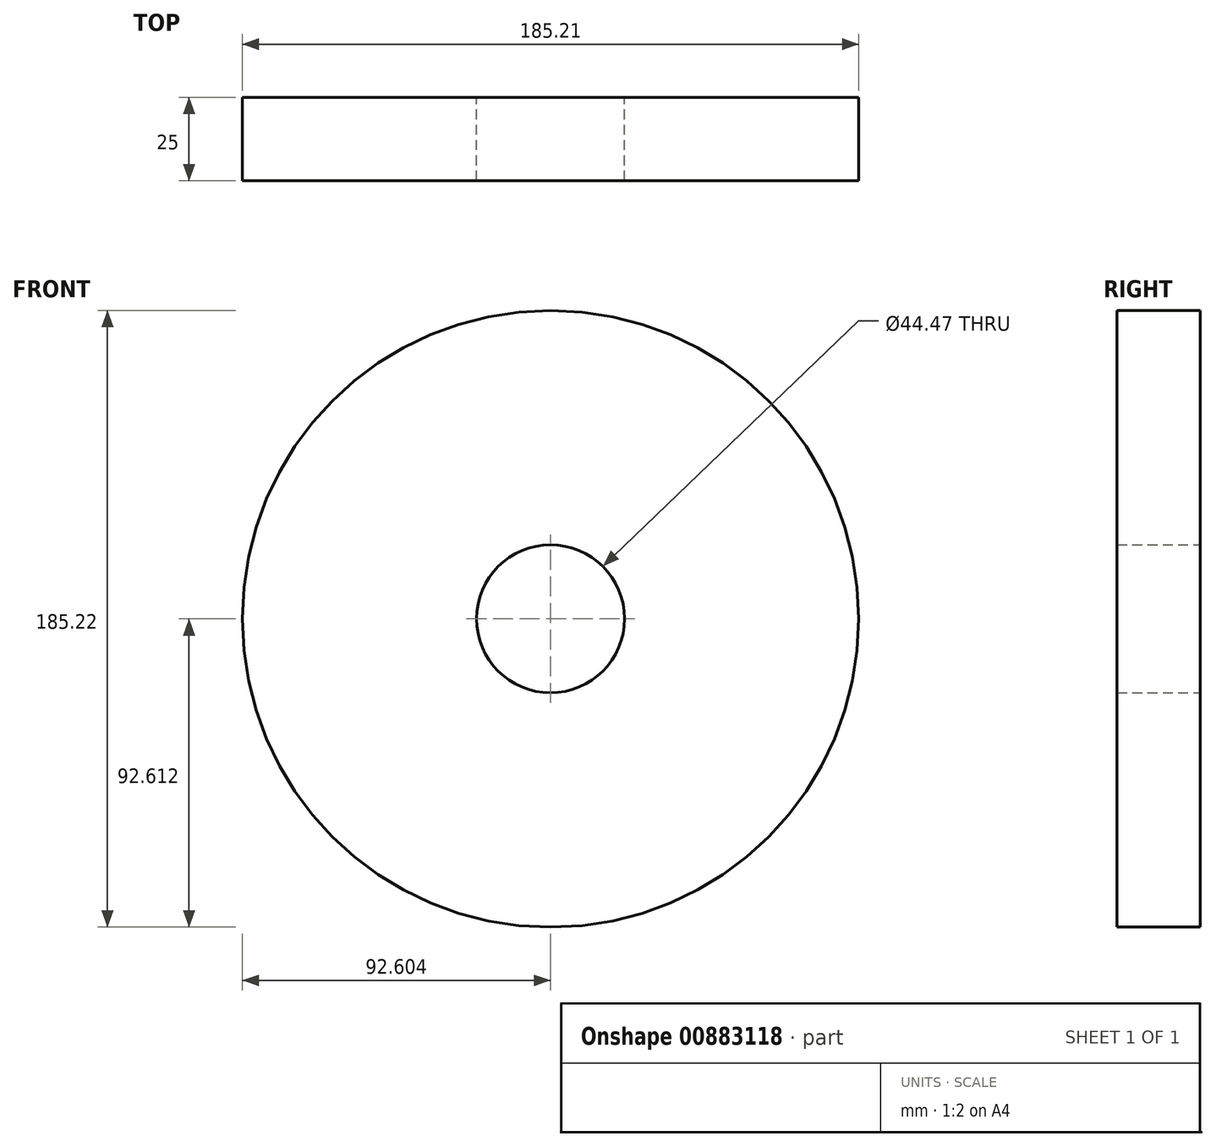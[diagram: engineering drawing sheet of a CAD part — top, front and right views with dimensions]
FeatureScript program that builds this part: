
annotation { "Feature Type Name" : "Feature", "Feature Type Description" : "" }
export const myFeature = defineFeature(function(context is Context, id is Id, definition is map)
    precondition{}
    {
        {
            var Q0;
            Q0=qCreatedBy(makeId("Front.planeOp"),FACE);
            var sketch = newSketch(context, id + "F0", { "sketchPlane" : qUnion([Q0])});
            skCircle(sketch, "E0", {"center": v(-56.56, 55.62) * mm, "radius": 4.14 * mm});
            skCircle(sketch, "E1", {"center": v(-56.56, 55.62) * mm, "radius": 22.23 * mm});
            skCircle(sketch, "E2", {"center": v(-56.56, 55.62) * mm, "radius": 92.6 * mm});
            skSolve(sketch);
        }
        {
            var Q0;
            Q0=makeQuery(id+"F0.imprint","IMPRINT",FACE,{"disambiguationData":[TD([[makeQuery(id+"F0.imprint","IMPRINT",EDGE,{"derivedFrom":sQuery(id+"F0.wireOp",EDGE,"E1")}),-1.0]])]});
            extrude(context, id + "F1", {"entities" : qUnion([Q0]), "depth" : 25 * mm, "offsetDistance" : 25 * mm});
        }
    });
